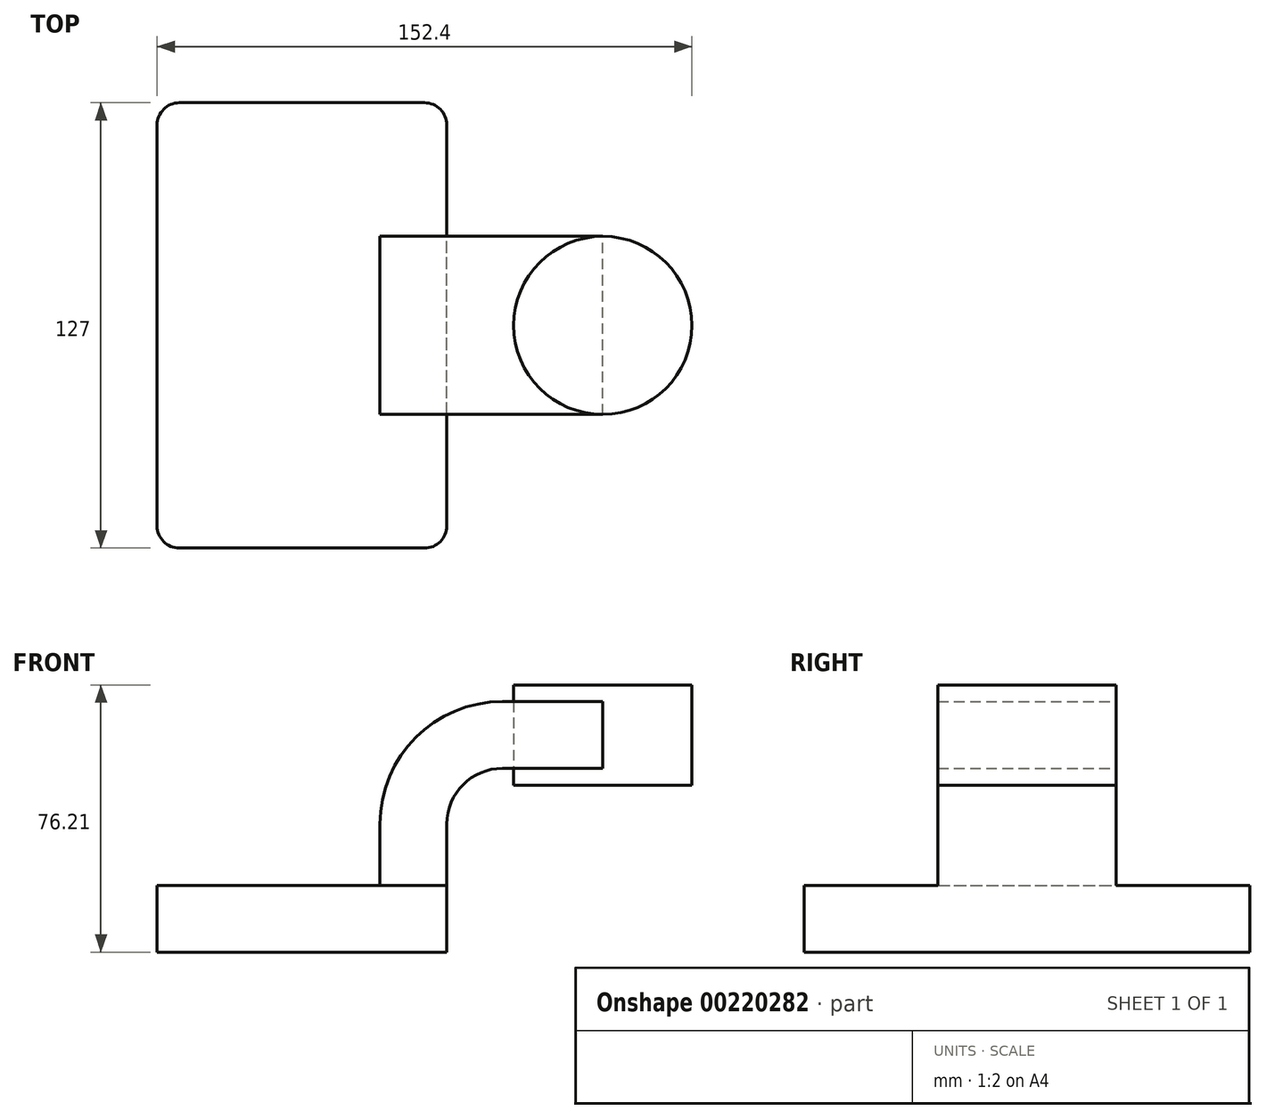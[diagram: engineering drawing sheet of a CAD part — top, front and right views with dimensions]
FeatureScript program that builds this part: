
annotation { "Feature Type Name" : "Feature", "Feature Type Description" : "" }
export const myFeature = defineFeature(function(context is Context, id is Id, definition is map)
    precondition{}
    {
        {
            var Q0;
            Q0=qCreatedBy(makeId("Front.planeOp"),FACE);
            var sketch = newSketch(context, id + "F0", { "sketchPlane" : qUnion([Q0])});
            skLineSegment(sketch, "E0.bottom", {"start": v(41.28, -9.53) * mm, "end": v(-41.28, -9.53) * mm});
            skLineSegment(sketch, "E0.top", {"start": v(41.28, 9.53) * mm, "end": v(-41.28, 9.52) * mm});
            skLineSegment(sketch, "E0.left", {"start": v(41.28, -9.53) * mm, "end": v(41.28, 9.53) * mm});
            skLineSegment(sketch, "E0.right", {"start": v(-41.28, -9.53) * mm, "end": v(-41.28, 9.52) * mm});
            skPoint(sketch, "E0.middle", {"position": v(0, 0) * mm});
            skLineSegment(sketch, "E1.bottom", {"start": v(111.12, 38.1) * mm, "end": v(60.32, 38.1) * mm});
            skLineSegment(sketch, "E1.top", {"start": v(111.12, 66.68) * mm, "end": v(60.32, 66.68) * mm});
            skLineSegment(sketch, "E1.left", {"start": v(111.12, 38.1) * mm, "end": v(111.12, 66.68) * mm});
            skLineSegment(sketch, "E1.right", {"start": v(60.32, 38.1) * mm, "end": v(60.32, 66.67) * mm});
            skPoint(sketch, "E1.middle", {"position": v(85.72, 52.39) * mm});
            skLineSegment(sketch, "E2", {"start": v(41.28, 9.53) * mm, "end": v(41.28, 27) * mm});
            skArc(sketch, "E3", {"start": v(41.28, 27) * mm, "mid": v(45.92, 38.23) * mm, "end": v(57.15, 42.88) * mm});
            skLineSegment(sketch, "E4", {"start": v(57.15, 42.88) * mm, "end": v(85.72, 42.88) * mm});
            skLineSegment(sketch, "E5.0", {"start": v(57.15, 61.93) * mm, "end": v(85.72, 61.93) * mm});
            skArc(sketch, "E5.1", {"start": v(22.23, 27) * mm, "mid": v(32.45, 51.7) * mm, "end": v(57.15, 61.93) * mm});
            skLineSegment(sketch, "E5.2", {"start": v(22.23, 9.52) * mm, "end": v(22.23, 27) * mm});
            skLineSegment(sketch, "E6", {"start": v(85.72, 38.1) * mm, "end": v(85.72, 66.68) * mm});
            skFitSpline(sketch, "E7", {"points": [v(-41.28, 9.52) * mm, v(57.15, 61.93) * mm], "startDerivative": vector(34.85, 101.97) * mm, "endDerivative": vector(148, -3.63) * mm});
            skSolve(sketch);
        }
        {
            var Q0;
            Q0=makeQuery(id+"F0.imprint","IMPRINT",FACE,{"disambiguationData":[TD([[makeQuery(id+"F0.imprint","IMPRINT",EDGE,{"derivedFrom":sQuery(id+"F0.wireOp",EDGE,"E0.bottom")}),-1.0]])]});
            extrude(context, id + "F1", {"entities" : qUnion([Q0]), "endBound" : BoundingType.SYMMETRIC, "depth" : 127 * mm});
        }
        {
            var Q0;
            {var subQ1=sQuery(id+"F0.wireOp",EDGE,"E2");Q0=makeQuery(id+"F0.imprint","IMPRINT",FACE,{"disambiguationData":[TD([[makeQuery(id+"F0.imprint","IMPRINT",EDGE,{"derivedFrom":subQ1}),1.0]])]});}
            var Q1;
            {var subQ0=sQuery(id+"F0.wireOp",EDGE,"E4");var subQ1=sQuery(id+"F0.wireOp",EDGE,"E1.right");var subQ2=makeQuery(id+"F0.imprint","INTERSECT",VERTEX,{"derivedFrom":[subQ1,subQ0]});Q1=makeQuery(id+"F0.imprint","IMPRINT",FACE,{"disambiguationData":[TD([[makeQuery(id+"F0.imprint","IMPRINT",EDGE,{"disambiguationData":[TD([[subQ2,-1.0]])],"derivedFrom":subQ1}),-1.0]])]});}
            extrude(context, id + "F2", {"entities" : qUnion([Q0, Q1]), "operationType" : NewBodyOperationType.ADD, "endBound" : BoundingType.SYMMETRIC, "depth" : 50.8 * mm});
        }
        {
            var Q0;
            Q0=makeQuery(id+"F0.imprint","IMPRINT",FACE,{"disambiguationData":[TD([[makeQuery(id+"F0.imprint","IMPRINT",EDGE,{"derivedFrom":sQuery(id+"F0.wireOp",EDGE,"E5.1")}),1.0]])]});
            extrude(context, id + "F3", {"entities" : qUnion([Q0]), "operationType" : NewBodyOperationType.ADD, "endBound" : BoundingType.SYMMETRIC, "depth" : 15.88 * mm});
        }
        {
            var Q0;
            {var subQ0=sQuery(id+"F0.wireOp",EDGE,"E1.left");Q0=makeQuery(id+"F0.imprint","IMPRINT",FACE,{"disambiguationData":[TD([[makeQuery(id+"F0.imprint","IMPRINT",EDGE,{"derivedFrom":subQ0}),1.0]])]});}
            var Q1;
            Q1=sQuery(id+"F0.wireOp",EDGE,"E6");
            revolve(context, id + "F4", {"entities" : qUnion([Q0]), "axis" : qUnion([Q1]), "revolveType" : RevolveType.FULL});
        }
        {
            var Q0;
            Q0=makeQuery(id+"F1.opExtrude","CAP_EDGE",EDGE,{"disambiguationData":[OSD([sQuery(id+"F0.wireOp",EDGE,"E0.left")])],"isStart":false});
            var Q1;
            Q1=makeQuery(id+"F1.opExtrude","CAP_EDGE",EDGE,{"disambiguationData":[OSD([sQuery(id+"F0.wireOp",EDGE,"E0.right")])],"isStart":false});
            var Q2;
            Q2=makeQuery(id+"F1.opExtrude","CAP_EDGE",EDGE,{"disambiguationData":[OSD([sQuery(id+"F0.wireOp",EDGE,"E0.right")])],"isStart":true});
            var Q3;
            Q3=makeQuery(id+"F1.opExtrude","CAP_EDGE",EDGE,{"disambiguationData":[OSD([sQuery(id+"F0.wireOp",EDGE,"E0.left")])],"isStart":true});
            fillet(context, id + "F5", {"entities" : qUnion([Q0, Q1, Q2, Q3]), "radius" : 6.35 * mm, "tangentPropagation" : true, "allowEdgeOverflow" : false});
        }
    });
